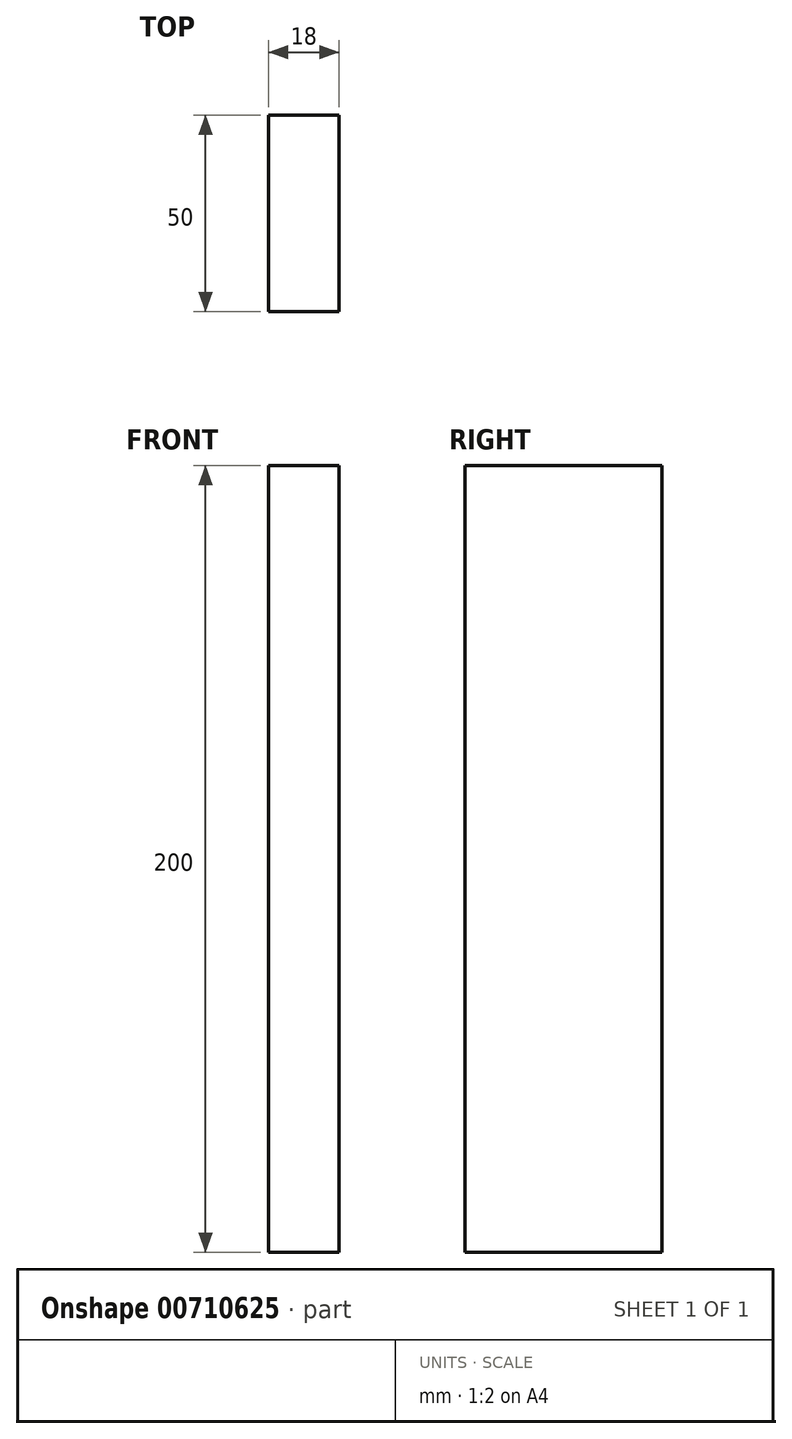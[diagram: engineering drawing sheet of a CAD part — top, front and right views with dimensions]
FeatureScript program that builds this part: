
annotation { "Feature Type Name" : "Feature", "Feature Type Description" : "" }
export const myFeature = defineFeature(function(context is Context, id is Id, definition is map)
    precondition{}
    {
        {
            var Q0;
            Q0=qCreatedBy(makeId("Front.planeOp"),FACE);
            var sketch = newSketch(context, id + "F0", { "sketchPlane" : qUnion([Q0])});
            skLineSegment(sketch, "E0.bottom", {"start": v(0, 0) * mm, "end": v(18, 0) * mm});
            skLineSegment(sketch, "E0.top", {"start": v(0, 200) * mm, "end": v(18, 200) * mm});
            skLineSegment(sketch, "E0.left", {"start": v(0, 0) * mm, "end": v(0, 200) * mm});
            skLineSegment(sketch, "E0.right", {"start": v(18, 0) * mm, "end": v(18, 200) * mm});
            skSolve(sketch);
        }
        {
            var Q0;
            Q0=makeQuery(id+"F0.imprint","IMPRINT",FACE,{"disambiguationData":[TD([[makeQuery(id+"F0.imprint","IMPRINT",EDGE,{"derivedFrom":sQuery(id+"F0.wireOp",EDGE,"E0.bottom")}),1.0]])]});
            extrude(context, id + "F1", {"entities" : qUnion([Q0]), "depth" : 50 * mm, "offsetDistance" : 25 * mm});
        }
    });
